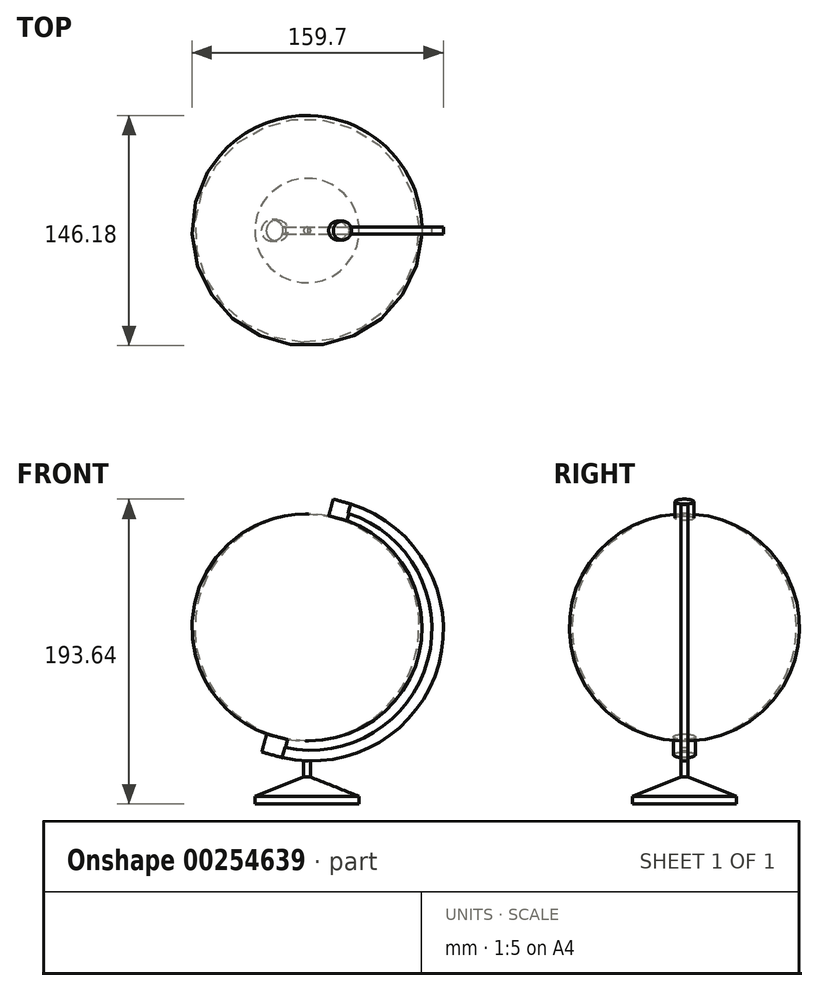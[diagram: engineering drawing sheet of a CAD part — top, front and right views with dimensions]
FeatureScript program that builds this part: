
annotation { "Feature Type Name" : "Feature", "Feature Type Description" : "" }
export const myFeature = defineFeature(function(context is Context, id is Id, definition is map)
    precondition{}
    {
        {
            var Q0;
            Q0=qCreatedBy(makeId("Front.planeOp"),FACE);
            var sketch = newSketch(context, id + "F0", { "sketchPlane" : qUnion([Q0])});
            skLineSegment(sketch, "E0", {"start": v(0, -72.17) * mm, "end": v(0, 71.92) * mm});
            skArc(sketch, "E1", {"start": v(0, -72.17) * mm, "mid": v(73.1, -0.13) * mm, "end": v(0, 71.92) * mm});
            skSolve(sketch);
        }
        {
            var Q0;
            Q0 = qSketchRegion(id + "F0", true);
            var Q1;
            Q1=sQuery(id+"F0.wireOp",EDGE,"E0");
            revolve(context, id + "F1", {"entities" : qUnion([Q0]), "axis" : qUnion([Q1]), "revolveType" : RevolveType.FULL});
        }
        {
            var Q0;
            Q0=qCreatedBy(makeId("Front.planeOp"),FACE);
            var sketch = newSketch(context, id + "F2", { "sketchPlane" : qUnion([Q0])});
            skLineSegment(sketch, "E2", {"start": v(-22.1, -81.07) * mm, "end": v(22.44, 79.78) * mm});
            skLineSegment(sketch, "E3", {"start": v(22.44, 79.78) * mm, "end": v(28.2, 78.18) * mm});
            skLineSegment(sketch, "E4", {"start": v(28.2, 78.18) * mm, "end": v(24.57, 65.1) * mm});
            skLineSegment(sketch, "E5", {"start": v(24.57, 65.1) * mm, "end": v(18.81, 66.69) * mm});
            skLineSegment(sketch, "E6", {"start": v(-22.1, -81.07) * mm, "end": v(-15.45, -82.92) * mm});
            skLineSegment(sketch, "E7", {"start": v(-15.45, -82.92) * mm, "end": v(-11.5, -68.62) * mm});
            skLineSegment(sketch, "E8", {"start": v(-11.5, -68.62) * mm, "end": v(-18.14, -66.78) * mm});
            skSolve(sketch);
        }
        {
            var Q0;
            Q0 = qSketchRegion(id + "F2", true);
            var Q1;
            Q1=sQuery(id+"F2.wireOp",EDGE,"E2");
            revolve(context, id + "F3", {"operationType" : NewBodyOperationType.ADD, "entities" : qUnion([Q0]), "axis" : qUnion([Q1]), "revolveType" : RevolveType.FULL});
        }
        {
            var Q0;
            Q0=qCreatedBy(makeId("Front.planeOp"),FACE);
            var sketch = newSketch(context, id + "F4", { "sketchPlane" : qUnion([Q0])});
            skLineSegment(sketch, "E9", {"start": v(27.78, 78.16) * mm, "end": v(26.05, 72.44) * mm});
            skLineSegment(sketch, "E10", {"start": v(-15.85, -82.66) * mm, "end": v(-14.14, -76.4) * mm});
            skArc(sketch, "E11", {"start": v(-15.85, -82.66) * mm, "mid": v(83.7, -23.34) * mm, "end": v(27.78, 78.16) * mm});
            skArc(sketch, "E12", {"start": v(-14.14, -76.4) * mm, "mid": v(76.67, -21.08) * mm, "end": v(26.05, 72.44) * mm});
            skSolve(sketch);
        }
        {
            var Q0;
            Q0=makeQuery(id+"F4.imprint","IMPRINT",FACE,{"disambiguationData":[TD([[makeQuery(id+"F4.imprint","IMPRINT",EDGE,{"derivedFrom":sQuery(id+"F4.wireOp",EDGE,"E9")}),1.0]])]});
            extrude(context, id + "F5", {"entities" : qUnion([Q0]), "operationType" : NewBodyOperationType.ADD, "endBound" : BoundingType.SYMMETRIC, "depth" : 4.57 * mm});
        }
        {
            var Q0;
            Q0=qCreatedBy(makeId("Right.planeOp"),FACE);
            var sketch = newSketch(context, id + "F6", { "sketchPlane" : qUnion([Q0])});
            skLineSegment(sketch, "E13", {"start": v(0, 0) * mm, "end": v(0, -112.27) * mm});
            skLineSegment(sketch, "E14", {"start": v(0, -112.27) * mm, "end": v(33.12, -112.27) * mm});
            skLineSegment(sketch, "E15", {"start": v(33.12, -112.27) * mm, "end": v(33.12, -107.46) * mm});
            skLineSegment(sketch, "E16", {"start": v(33.12, -107.46) * mm, "end": v(0, -94.25) * mm});
            skLineSegment(sketch, "E17", {"start": v(0, -94.25) * mm, "end": v(2.13, -95.1) * mm});
            skLineSegment(sketch, "E18", {"start": v(2.13, -95.1) * mm, "end": v(2.13, -84.84) * mm});
            skLineSegment(sketch, "E19", {"start": v(2.13, -84.84) * mm, "end": v(0, -84.84) * mm});
            skSolve(sketch);
        }
        {
            var Q0;
            Q0 = qSketchRegion(id + "F6", true);
            var Q1;
            Q1=sQuery(id+"F6.wireOp",EDGE,"E13");
            revolve(context, id + "F7", {"operationType" : NewBodyOperationType.ADD, "entities" : qUnion([Q0]), "axis" : qUnion([Q1]), "revolveType" : RevolveType.FULL});
        }
    });
